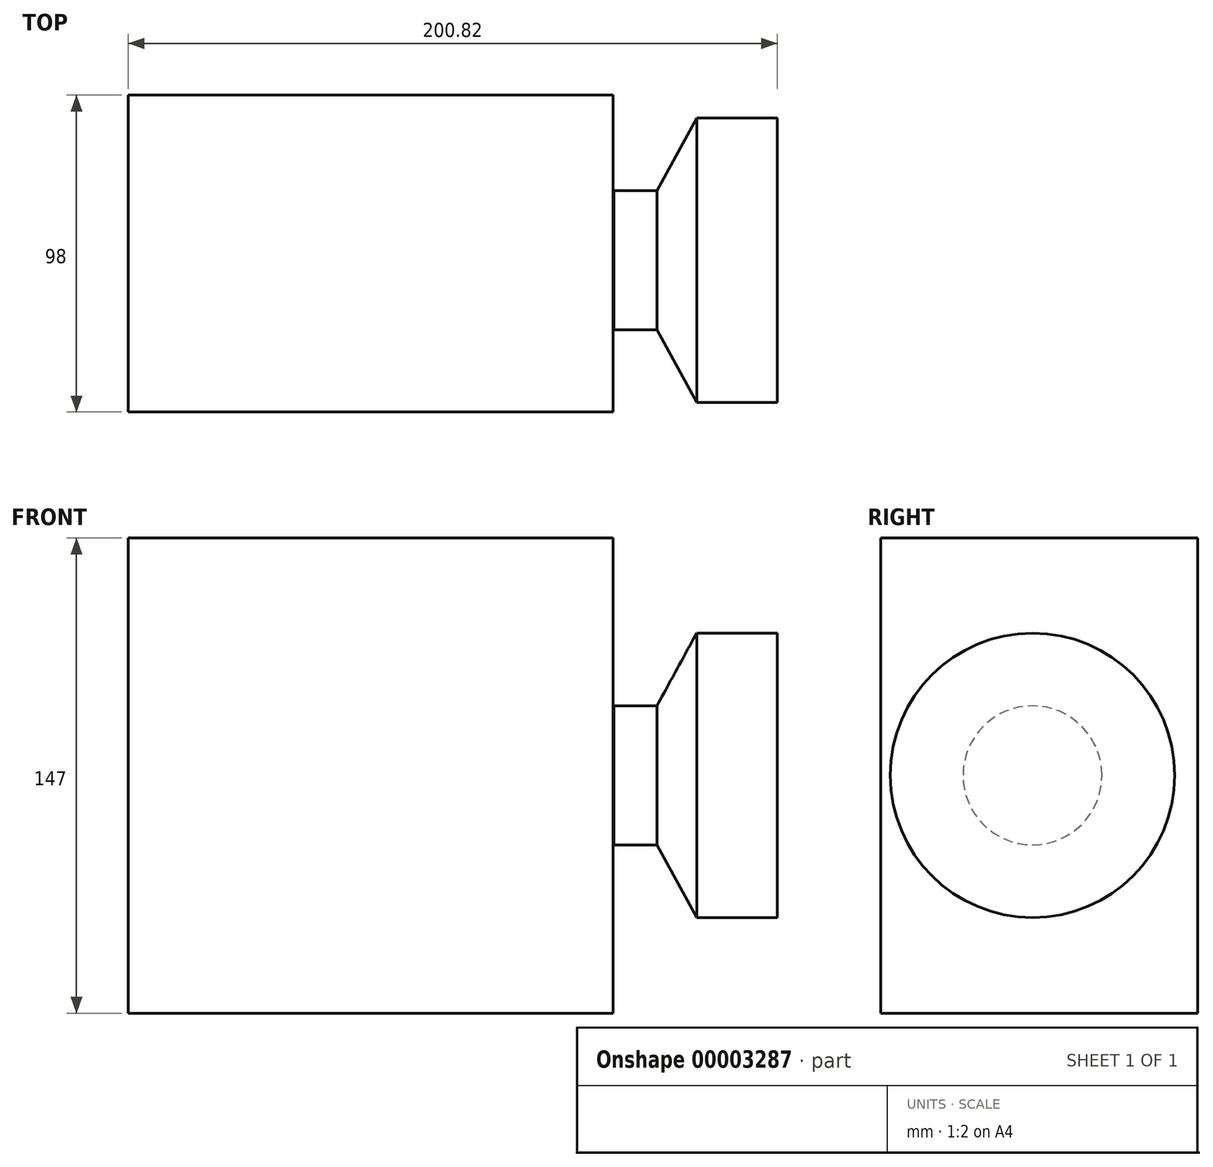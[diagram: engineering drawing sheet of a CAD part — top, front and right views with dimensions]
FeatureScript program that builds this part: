
annotation { "Feature Type Name" : "Feature", "Feature Type Description" : "" }
export const myFeature = defineFeature(function(context is Context, id is Id, definition is map)
    precondition{}
    {
        {
            var Q0;
            Q0=qCreatedBy(makeId("Top.planeOp"),FACE);
            var sketch = newSketch(context, id + "F0", { "sketchPlane" : qUnion([Q0])});
            skLineSegment(sketch, "E0.bottom", {"start": v(-75.06, 51.07) * mm, "end": v(74.94, 51.07) * mm});
            skLineSegment(sketch, "E0.top", {"start": v(-75.06, -46.93) * mm, "end": v(74.94, -46.93) * mm});
            skLineSegment(sketch, "E0.left", {"start": v(-75.06, 51.07) * mm, "end": v(-75.06, -46.93) * mm});
            skLineSegment(sketch, "E0.right", {"start": v(74.94, 51.07) * mm, "end": v(74.94, -46.93) * mm});
            skSolve(sketch);
        }
        {
            var Q0;
            Q0=makeQuery(id+"F0.imprint","IMPRINT",FACE,{"disambiguationData":[TD([[makeQuery(id+"F0.imprint","IMPRINT",EDGE,{"derivedFrom":sQuery(id+"F0.wireOp",EDGE,"E0.bottom")}),-1.0]])]});
            extrude(context, id + "F1", {"entities" : qUnion([Q0]), "depth" : 147 * mm, "symmetric" : true});
        }
        {
            var Q0;
            Q0=qCreatedBy(makeId("Front.planeOp"),FACE);
            var sketch = newSketch(context, id + "F2", { "sketchPlane" : qUnion([Q0])});
            skLineSegment(sketch, "E1", {"start": v(75.14, 21.56) * mm, "end": v(88.5, 21.56) * mm});
            skLineSegment(sketch, "E2", {"start": v(100.78, 44.06) * mm, "end": v(88.5, 21.56) * mm});
            skLineSegment(sketch, "E3", {"start": v(100.78, 44.06) * mm, "end": v(125.76, 44.06) * mm});
            skLineSegment(sketch, "E4", {"start": v(64.74, 0.07) * mm, "end": v(114.43, 0.07) * mm, "construction": true});
            skLineSegment(sketch, "E5", {"start": v(75.14, 21.56) * mm, "end": v(75.14, 0.07) * mm});
            skLineSegment(sketch, "E6", {"start": v(125.76, 44.06) * mm, "end": v(125.76, 0.07) * mm});
            skLineSegment(sketch, "E7", {"start": v(75.14, 0.07) * mm, "end": v(125.76, 0.07) * mm});
            skSolve(sketch);
        }
        {
            var Q0;
            Q0=makeQuery(id+"F2.imprint","IMPRINT",FACE,{"disambiguationData":[TD([[makeQuery(id+"F2.imprint","IMPRINT",EDGE,{"derivedFrom":sQuery(id+"F2.wireOp",EDGE,"E1")}),-1.0]])]});
            var Q1;
            Q1=sQuery(id+"F2.wireOp",EDGE,"E5");
            var Q2;
            Q2=sQuery(id+"F2.wireOp",EDGE,"E1");
            var Q3;
            Q3=sQuery(id+"F2.wireOp",EDGE,"E2");
            var Q4;
            Q4=sQuery(id+"F2.wireOp",EDGE,"E3");
            var Q5;
            Q5=sQuery(id+"F2.wireOp",EDGE,"E6");
            var Q6;
            Q6=sQuery(id+"F2.wireOp",EDGE,"E4");
            revolve(context, id + "F3", {"entities" : qUnion([Q0]), "surfaceEntities" : qUnion([Q1, Q2, Q3, Q4, Q5]), "axis" : qUnion([Q6]), "revolveType" : RevolveType.FULL});
        }
    });
